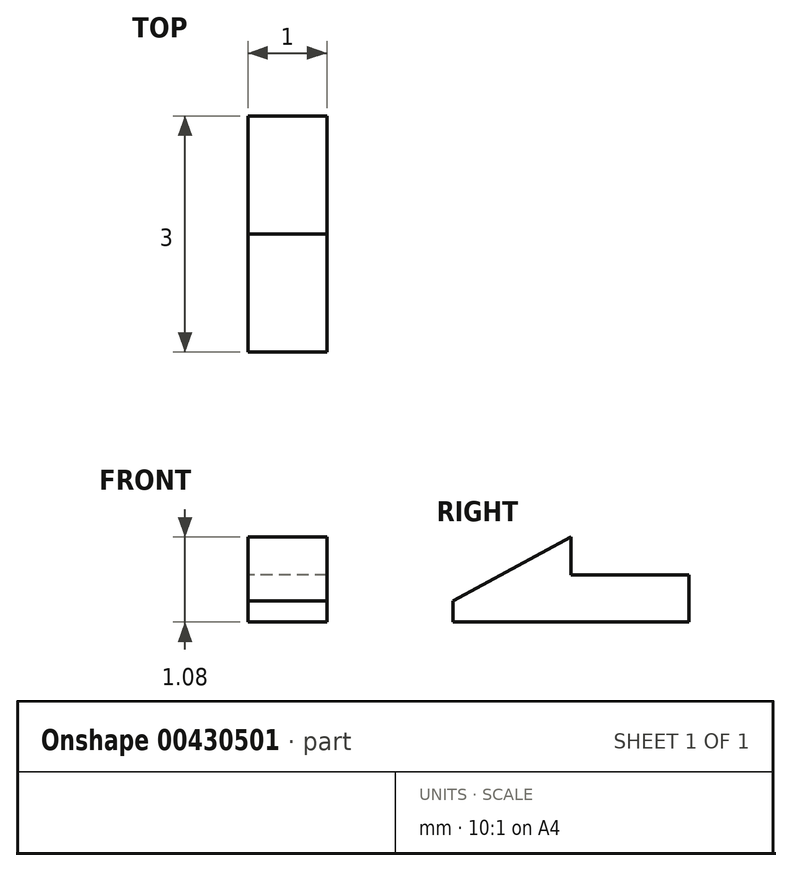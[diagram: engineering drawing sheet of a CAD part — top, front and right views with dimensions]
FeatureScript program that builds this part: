
annotation { "Feature Type Name" : "Feature", "Feature Type Description" : "" }
export const myFeature = defineFeature(function(context is Context, id is Id, definition is map)
    precondition{}
    {
        {
            var Q0;
            Q0=qCreatedBy(makeId("Right.planeOp"),FACE);
            var sketch = newSketch(context, id + "F0", { "sketchPlane" : qUnion([Q0])});
            skLineSegment(sketch, "E0", {"start": v(0, 1.08) * mm, "end": v(-1.5, 0.27) * mm});
            skLineSegment(sketch, "E1", {"start": v(-1.5, 0.27) * mm, "end": v(-1.5, 0) * mm});
            skLineSegment(sketch, "E2", {"start": v(-1.5, 0) * mm, "end": v(1.5, 0) * mm});
            skLineSegment(sketch, "E3", {"start": v(1.5, 0) * mm, "end": v(1.5, 0.6) * mm});
            skLineSegment(sketch, "E4", {"start": v(1.5, 0.6) * mm, "end": v(0, 0.6) * mm});
            skLineSegment(sketch, "E5", {"start": v(0, 0.6) * mm, "end": v(0, 1.08) * mm});
            skSolve(sketch);
        }
        {
            var Q0;
            Q0 = qSketchRegion(id + "F0", true);
            extrude(context, id + "F1", {"entities" : qUnion([Q0]), "depth" : 1 * mm});
        }
    });
